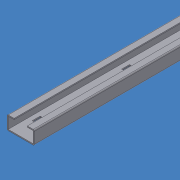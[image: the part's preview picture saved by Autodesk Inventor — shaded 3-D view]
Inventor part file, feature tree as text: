
AUTODESK INVENTOR PART (.ipt)
format: ipt  version: 2015 SP1 (Build 190203100, 203)  size: 249,344 bytes
history: native  units: mm
features: sheet_metal_op x9, other x8, sketch x6, plane x2
ambient origin geometry x8: Origin, YZ Plane, XZ Plane, XY Plane, X Axis, Y Axis, Z Axis, Center Point
bodies: Solid1 (feature_tree)
feature tree (25):
  sheet_metal_op  "Face1"
  sheet_metal_op  "Flange1"
  sheet_metal_op  "Flange2"
  sheet_metal_op  "Flange3"
  sheet_metal_op  "Flange4"
  plane  "Work Plane4"
  plane  "Work Plane6"
  sketch  "Sketch1"  dims[d4=0.001mm]
  other  "Plate1"
  sketch  "Sketch2"  dims[d5=3.0mm]
  other  "Plate2"
  sheet_metal_op  "Bend1"
  sketch  "Sketch3"  dims[d6=0.001mm]
  other  "Plate3"
  sheet_metal_op  "Bend2"
  sketch  "Sketch4"  dims[d7=6.0mm]
  other  "Plate4"
  sheet_metal_op  "Bend3"
  sketch  "Sketch5"  dims[d8=0.001mm]
  other  "Plate5"
  sheet_metal_op  "Bend4"
  sketch  "Sketch6"  dims[d9=29.0mm d10=90.0deg d11=0.001mm d12=3.0mm d13=0.001mm d14=6.0mm d15=0.001mm d16=29.0mm d17=90.0deg d18=0.001mm d19=3.0mm d20=0.001mm d21=6.0mm d22=0.001mm d23=15.0mm d24=90.0deg d25=0.001mm d26=3.0mm d27=0.001mm d28=6.0mm d29=0.001mm d30=15.0mm d31=90.0deg d32=0.001mm d33=4.0mm d34=20.5mm d35=4.0mm d36=20.5mm d37=0.0mm d38=33.0mm d40=4.0mm d41=0.0mm d42=450.0mm d45=150.0mm d46=10.0mm d47=10.0mm d48=64.0mm d49=6.0mm d50=64.0mm d51=4.0mm d52=9.0mm d62=20.5mm d63=4.0mm d64=9.0mm d65=20.5mm d66=4.0mm d68=4.0mm d69=0.0mm d71=50.0mm d72=33.0mm d73=16.5mm d0=3.0mm]
  other  "FlatPattern"
  other  "Cut1"
  other  "FlatPatternExtrusion2"
